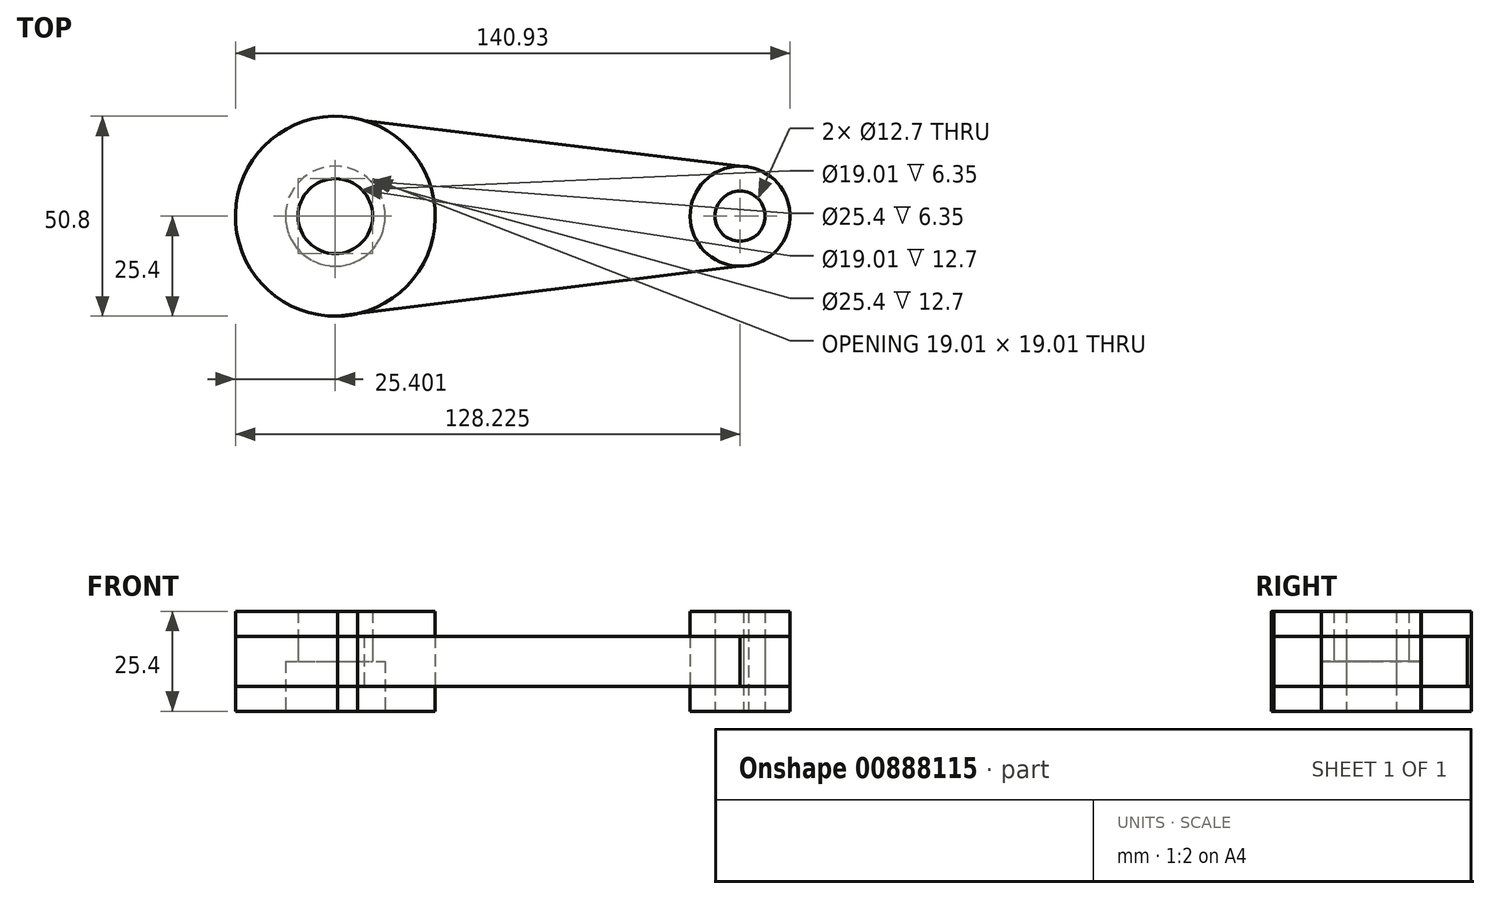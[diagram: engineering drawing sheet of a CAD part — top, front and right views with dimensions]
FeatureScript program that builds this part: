
annotation { "Feature Type Name" : "Feature", "Feature Type Description" : "" }
export const myFeature = defineFeature(function(context is Context, id is Id, definition is map)
    precondition{}
    {
        {
            var Q0;
            Q0=qCreatedBy(makeId("Top.planeOp"),FACE);
            var sketch = newSketch(context, id + "F0", { "sketchPlane" : qUnion([Q0])});
            skCircle(sketch, "E0", {"center": v(-68.75, 0) * mm, "radius": 25.4 * mm});
            skCircle(sketch, "E1", {"center": v(34.08, 0) * mm, "radius": 12.7 * mm});
            skLineSegment(sketch, "E2", {"start": v(-61.5, 24.34) * mm, "end": v(36.2, 12.52) * mm});
            skLineSegment(sketch, "E3", {"start": v(-68.19, -25.4) * mm, "end": v(34.08, -12.7) * mm});
            skCircle(sketch, "E4", {"center": v(-68.75, 0) * mm, "radius": 9.5 * mm});
            skCircle(sketch, "E5", {"center": v(34.08, 0) * mm, "radius": 6.35 * mm});
            skSolve(sketch);
        }
        {
            var Q0;
            Q0=makeQuery(id+"F0.imprint","IMPRINT",FACE,{"disambiguationData":[TD([[makeQuery(id+"F0.imprint","IMPRINT",EDGE,{"derivedFrom":sQuery(id+"F0.wireOp",EDGE,"E4")}),-1.0]])]});
            var Q1;
            Q1=makeQuery(id+"F0.imprint","IMPRINT",FACE,{"disambiguationData":[TD([[makeQuery(id+"F0.imprint","IMPRINT",EDGE,{"derivedFrom":sQuery(id+"F0.wireOp",EDGE,"E5")}),-1.0]])]});
            extrude(context, id + "F1", {"entities" : qUnion([Q0, Q1]), "depth" : 12.7 * mm, "offsetDistance" : 25.4 * mm, "hasSecondDirection" : true, "secondDirectionOppositeDirection" : true, "secondDirectionDepth" : 12.7 * mm});
        }
        {
            var Q0;
            Q0 = qSketchRegion(id + "F0", true);
            extrude(context, id + "F2", {"entities" : qUnion([Q0]), "depth" : 6.35 * mm, "offsetDistance" : 25.4 * mm, "hasSecondDirection" : true, "secondDirectionOppositeDirection" : true, "secondDirectionDepth" : 6.35 * mm});
        }
        {
            var Q0;
            Q0=makeQuery(id+"F1.opExtrude","CAP_FACE",FACE,{"disambiguationData":[OSD([sQuery(id+"F0.wireOp",EDGE,"E0"),sQuery(id+"F0.wireOp",EDGE,"E3"),sQuery(id+"F0.wireOp",EDGE,"E4")])],"isStart":true});
            var sketch = newSketch(context, id + "F3", { "sketchPlane" : qUnion([Q0])});
            skCircle(sketch, "E6", {"center": v(-68.75, 0) * mm, "radius": 12.7 * mm});
            skSolve(sketch);
        }
        {
            var Q0;
            Q0 = qSketchRegion(id + "F3", true);
            extrude(context, id + "F4", {"entities" : qUnion([Q0]), "operationType" : NewBodyOperationType.REMOVE, "oppositeDirection" : true, "depth" : 12.7 * mm, "offsetDistance" : 25.4 * mm});
        }
    });
